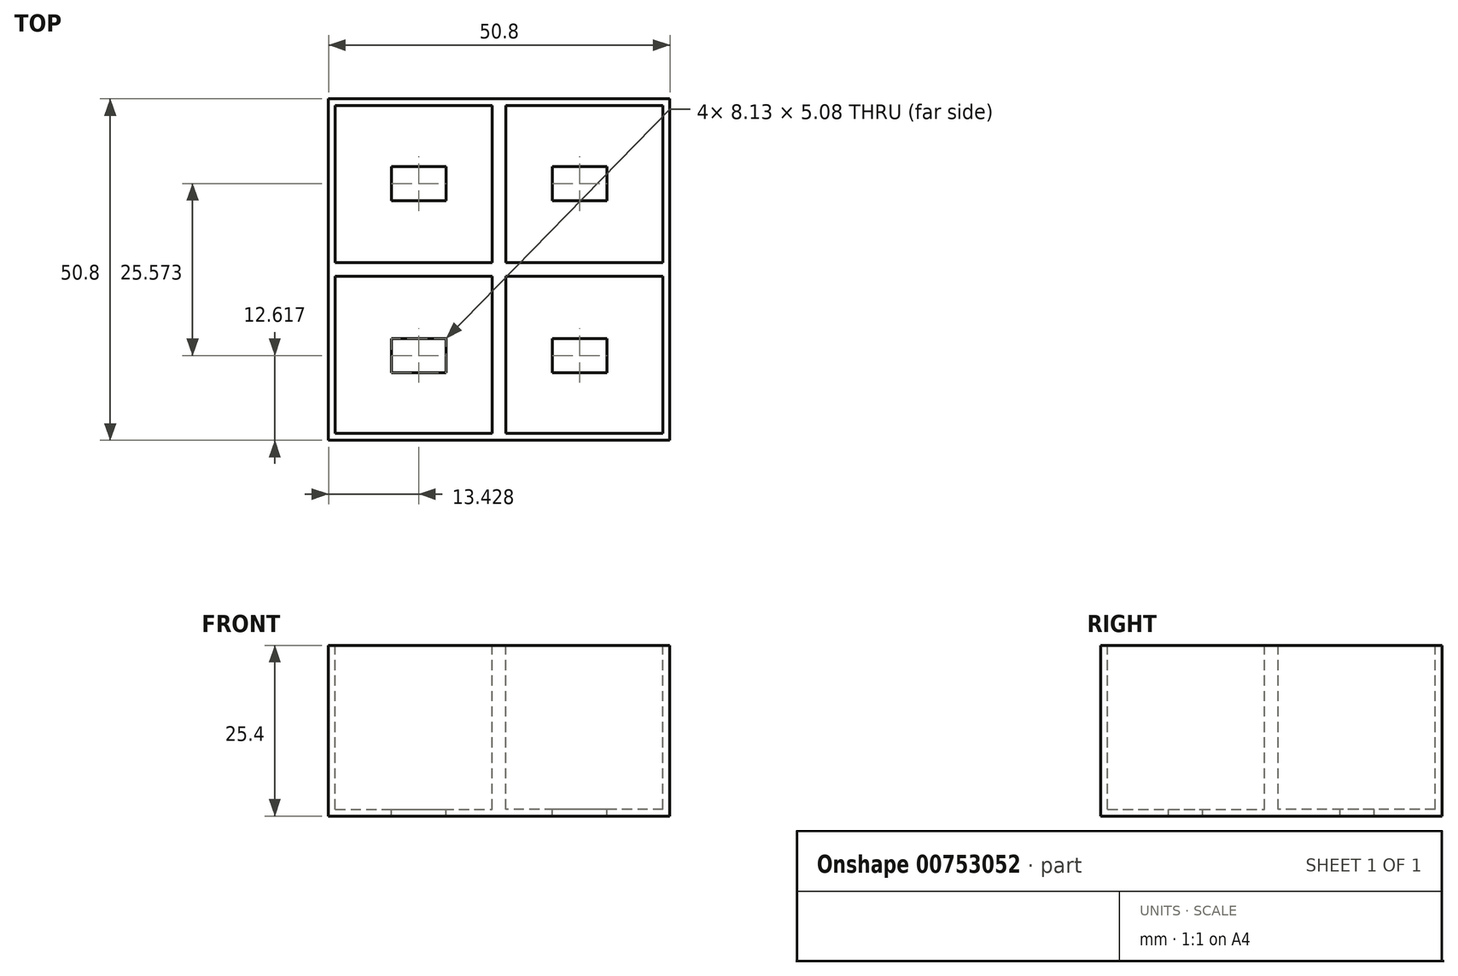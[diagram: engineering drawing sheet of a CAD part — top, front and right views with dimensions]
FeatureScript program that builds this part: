
annotation { "Feature Type Name" : "Feature", "Feature Type Description" : "" }
export const myFeature = defineFeature(function(context is Context, id is Id, definition is map)
    precondition{}
    {
        {
            var Q0;
            Q0=qCreatedBy(makeId("Top.planeOp"),FACE);
            var sketch = newSketch(context, id + "F0", { "sketchPlane" : qUnion([Q0])});
            skLineSegment(sketch, "E0.bottom", {"start": v(-37.88, -0.02) * mm, "end": v(-12.48, -0.02) * mm});
            skLineSegment(sketch, "E0.top", {"start": v(-37.88, -25.42) * mm, "end": v(-12.48, -25.42) * mm});
            skLineSegment(sketch, "E0.left", {"start": v(-37.88, -0.02) * mm, "end": v(-37.88, -25.42) * mm});
            skLineSegment(sketch, "E0.right", {"start": v(-12.48, -0.02) * mm, "end": v(-12.48, -25.42) * mm});
            skSolve(sketch);
        }
        {
            var Q0;
            Q0=makeQuery(id+"F0.imprint","IMPRINT",FACE,{"disambiguationData":[TD([[makeQuery(id+"F0.imprint","IMPRINT",EDGE,{"derivedFrom":sQuery(id+"F0.wireOp",EDGE,"E0.bottom")}),-1.0]])]});
            extrude(context, id + "F1", {"entities" : qUnion([Q0]), "oppositeDirection" : true, "depth" : 25.4 * mm, "offsetDistance" : 25.4 * mm});
        }
        {
            var Q0;
            Q0=makeQuery(id+"F1.opExtrude","CAP_FACE",FACE,{"disambiguationData":[OSD([sQuery(id+"F0.wireOp",EDGE,"E0.bottom"),sQuery(id+"F0.wireOp",EDGE,"E0.top"),sQuery(id+"F0.wireOp",EDGE,"E0.left"),sQuery(id+"F0.wireOp",EDGE,"E0.right")])],"isStart":true});
            shell(context, id + "F2", {"entities" : qUnion([Q0]), "thickness" : 1.02 * mm});
        }
        {
            var Q0;
            Q0=qCreatedBy(makeId("Top.planeOp"),FACE);
            var sketch = newSketch(context, id + "F3", { "sketchPlane" : qUnion([Q0])});
            skLineSegment(sketch, "E1.bottom", {"start": v(-28.52, -10.1) * mm, "end": v(-20.39, -10.1) * mm});
            skLineSegment(sketch, "E1.top", {"start": v(-28.52, -15.17) * mm, "end": v(-20.39, -15.17) * mm});
            skLineSegment(sketch, "E1.left", {"start": v(-28.52, -10.1) * mm, "end": v(-28.52, -15.17) * mm});
            skLineSegment(sketch, "E1.right", {"start": v(-20.39, -10.1) * mm, "end": v(-20.39, -15.17) * mm});
            skSolve(sketch);
        }
        {
            var Q0;
            Q0=makeQuery(id+"F3.imprint","IMPRINT",FACE,{"disambiguationData":[TD([[makeQuery(id+"F3.imprint","IMPRINT",EDGE,{"derivedFrom":sQuery(id+"F3.wireOp",EDGE,"E1.bottom")}),-1.0]])]});
            extrude(context, id + "F4", {"entities" : qUnion([Q0]), "operationType" : NewBodyOperationType.REMOVE, "oppositeDirection" : true, "depth" : 25.4 * mm, "offsetDistance" : 25.4 * mm});
        }
        {
            var Q0;
            Q0=makeQuery(id+"F1.opExtrude","SWEPT_BODY",BODY,{"disambiguationData":[OSD([sQuery(id+"F0.wireOp",EDGE,"E0.bottom"),sQuery(id+"F0.wireOp",EDGE,"E0.top"),sQuery(id+"F0.wireOp",EDGE,"E0.left"),sQuery(id+"F0.wireOp",EDGE,"E0.right")])]});
            var Q1;
            Q1=makeQuery(id+"F1.opExtrude","SWEPT_FACE",FACE,{"disambiguationData":[OSD([sQuery(id+"F0.wireOp",EDGE,"E0.right")])]});
            mirror(context, id + "F5", {"operationType" : NewBodyOperationType.ADD, "entities" : qUnion([Q0]), "mirrorPlane" : qUnion([Q1])});
        }
        {
            var Q0;
            Q0=makeQuery(id+"F1.opExtrude","SWEPT_BODY",BODY,{"disambiguationData":[OSD([sQuery(id+"F0.wireOp",EDGE,"E0.bottom"),sQuery(id+"F0.wireOp",EDGE,"E0.top"),sQuery(id+"F0.wireOp",EDGE,"E0.left"),sQuery(id+"F0.wireOp",EDGE,"E0.right")])]});
            var Q1;
            {var subQ0=makeQuery(id+"F1.opExtrude","SWEPT_FACE",FACE,{"disambiguationData":[OSD([sQuery(id+"F0.wireOp",EDGE,"E0.top")])]});Q1=makeQuery(id+"F5.boolean.opBoolean","MERGE",FACE,{"derivedFrom":[subQ0,makeQuery(id+"F5.opPattern","COPY",FACE,{"derivedFrom":subQ0,"instanceName":"1"})]});}
            mirror(context, id + "F6", {"operationType" : NewBodyOperationType.ADD, "entities" : qUnion([Q0]), "mirrorPlane" : qUnion([Q1])});
        }
    });
